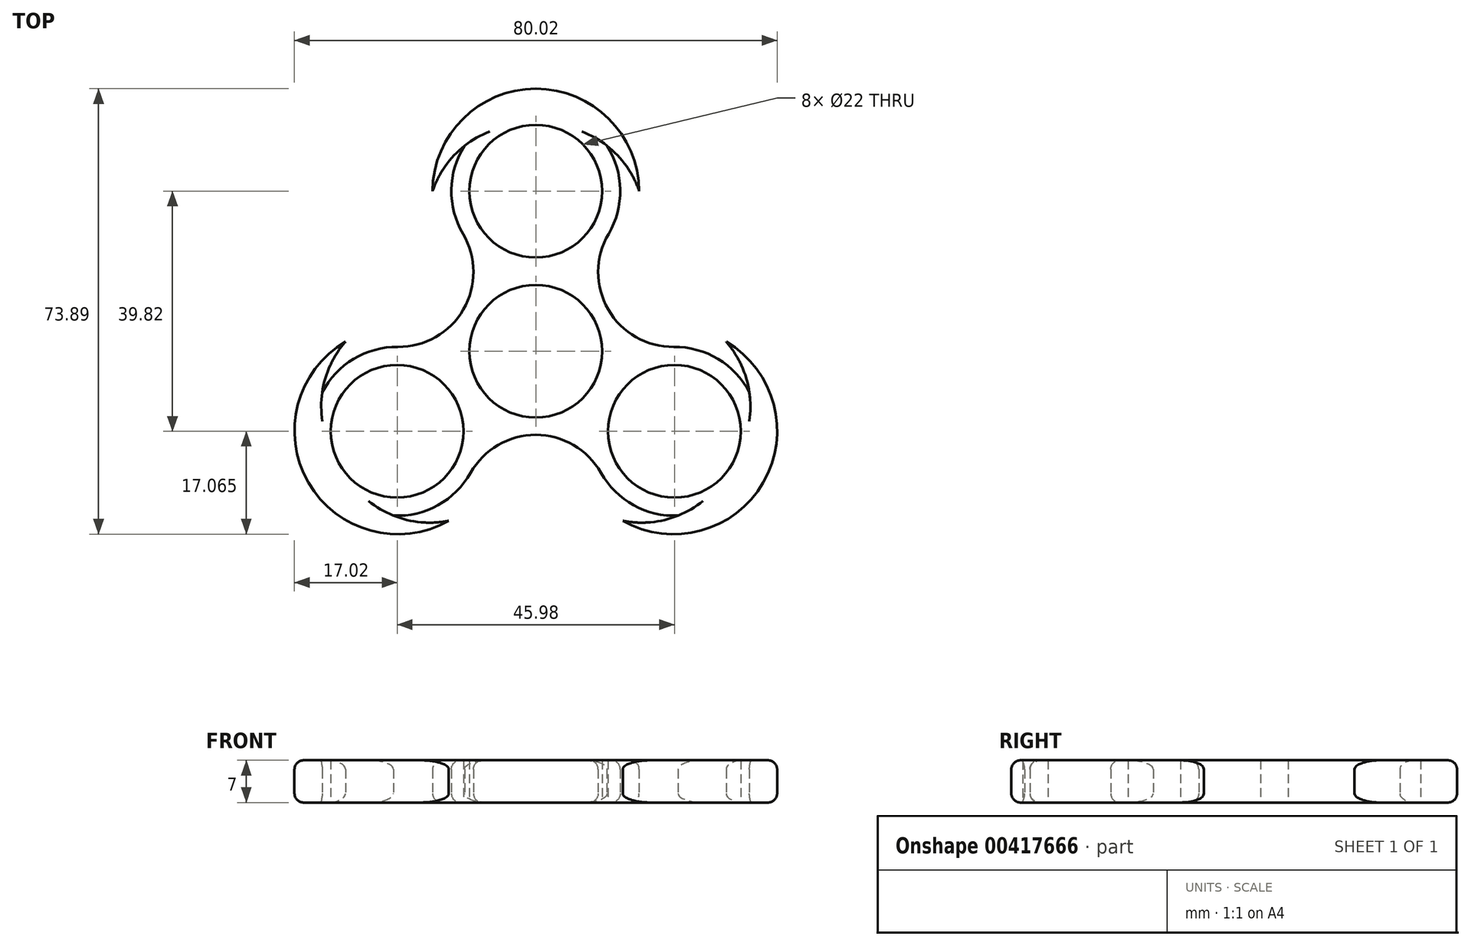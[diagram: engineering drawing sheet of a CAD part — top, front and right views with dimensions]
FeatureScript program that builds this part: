
annotation { "Feature Type Name" : "Feature", "Feature Type Description" : "" }
export const myFeature = defineFeature(function(context is Context, id is Id, definition is map)
    precondition{}
    {
        {
            var Q0;
            Q0=qCreatedBy(makeId("Top.planeOp"),FACE);
            var sketch = newSketch(context, id + "F0", { "sketchPlane" : qUnion([Q0])});
            skPoint(sketch, "E0", {"position": v(-7.78, 43.65) * mm});
            skPoint(sketch, "E1", {"position": v(7.78, 43.65) * mm});
            skLineSegment(sketch, "E2", {"start": v(-11.8, 43.4) * mm, "end": v(-11.8, 43.4) * mm});
            skArc(sketch, "E3", {"start": v(-11.8, 43.4) * mm, "mid": v(-14, 36.12) * mm, "end": v(-12.06, 28.77) * mm});
            skArc(sketch, "E4", {"start": v(7.78, 43.65) * mm, "mid": v(0, 46.88) * mm, "end": v(-7.78, 43.65) * mm});
            skArc(sketch, "E5", {"start": v(-7.78, 43.65) * mm, "mid": v(0, 24.88) * mm, "end": v(7.78, 43.65) * mm});
            skPoint(sketch, "E6.center", {"position": v(0, 0) * mm});
            skPoint(sketch, "E7", {"position": v(0, 56.88) * mm});
            skCircle(sketch, "E8", {"center": v(0, 9.33) * mm, "radius": 11 * mm});
            skArc(sketch, "E9.1.0", {"start": v(-23.6, -17.93) * mm, "mid": v(-16.2, -16.2) * mm, "end": v(-10.8, -10.84) * mm});
            skArc(sketch, "E9.1.1", {"start": v(-25.84, -14.57) * mm, "mid": v(-13.46, 1.55) * mm, "end": v(-33.62, -1.1) * mm});
            skArc(sketch, "E9.1.2", {"start": v(-33.62, -1.1) * mm, "mid": v(-32.52, -9.45) * mm, "end": v(-25.84, -14.57) * mm});
            skArc(sketch, "E9.2.0", {"start": v(35.41, 2.51) * mm, "mid": v(30.2, 8.05) * mm, "end": v(22.87, 10.05) * mm});
            skArc(sketch, "E9.2.1", {"start": v(33.62, -1.1) * mm, "mid": v(13.46, 1.55) * mm, "end": v(25.84, -14.57) * mm});
            skArc(sketch, "E9.2.2", {"start": v(25.84, -14.57) * mm, "mid": v(32.52, -9.45) * mm, "end": v(33.62, -1.1) * mm});
            skArc(sketch, "E10", {"start": v(8.99, 30.58) * mm, "mid": v(8.87, 29.9) * mm, "end": v(8.77, 29.24) * mm});
            skArc(sketch, "E11.1.0", {"start": v(13.91, -9.08) * mm, "mid": v(13.4, -8.64) * mm, "end": v(12.86, -8.22) * mm});
            skLineSegment(sketch, "E11.anchor1", {"start": v(0, 9.33) * mm, "end": v(22.9, 6.48) * mm, "construction": true});
            skLineSegment(sketch, "E11.anchor2", {"start": v(0, 9.33) * mm, "end": v(-8.99, 30.58) * mm, "construction": true});
            skLineSegment(sketch, "E12", {"start": v(0, 35.87) * mm, "end": v(8.99, 30.58) * mm});
            skLineSegment(sketch, "E13", {"start": v(8.99, 30.58) * mm, "end": v(9.48, 30.3) * mm});
            skLineSegment(sketch, "E14.MirrorCS", {"start": v(0, 35.87) * mm, "end": v(-8.99, 30.58) * mm});
            skLineSegment(sketch, "E15.1.0", {"start": v(-23, -3.95) * mm, "end": v(-22.9, 6.48) * mm});
            skLineSegment(sketch, "E15.1.1", {"start": v(-23, -3.95) * mm, "end": v(-13.91, -9.08) * mm});
            skLineSegment(sketch, "E15.1.2", {"start": v(-13.91, -9.08) * mm, "end": v(-13.42, -9.36) * mm});
            skLineSegment(sketch, "E15.1.3", {"start": v(-22.9, 6.48) * mm, "end": v(-22.87, 10.05) * mm});
            skLineSegment(sketch, "E15.2.0", {"start": v(23, -3.95) * mm, "end": v(13.91, -9.08) * mm});
            skLineSegment(sketch, "E15.2.1", {"start": v(23, -3.95) * mm, "end": v(22.9, 6.48) * mm});
            skLineSegment(sketch, "E15.2.2", {"start": v(22.9, 6.48) * mm, "end": v(22.87, 10.05) * mm});
            skLineSegment(sketch, "E15.2.3", {"start": v(13.91, -9.08) * mm, "end": v(10.8, -10.84) * mm});
            skArc(sketch, "E16.trimOffspring", {"start": v(-8.66, 24.88) * mm, "mid": v(-7.3, 23.93) * mm, "end": v(-5.85, 23.15) * mm});
            skArc(sketch, "E17.trimOffspring", {"start": v(-22.87, 10.05) * mm, "mid": v(-30.2, 8.05) * mm, "end": v(-35.41, 2.51) * mm});
            skArc(sketch, "E18", {"start": v(-12.06, 28.77) * mm, "mid": v(-12, 16.26) * mm, "end": v(-22.87, 10.05) * mm});
            skArc(sketch, "E19.trimOffspring", {"start": v(12.06, 28.77) * mm, "mid": v(14, 36.12) * mm, "end": v(11.8, 43.4) * mm});
            skArc(sketch, "E20.trimOffspring", {"start": v(21.63, 6.97) * mm, "mid": v(22.26, 6.72) * mm, "end": v(22.9, 6.48) * mm});
            skArc(sketch, "E21.trimOffspring", {"start": v(-12.86, -8.22) * mm, "mid": v(-13.4, -8.64) * mm, "end": v(-13.91, -9.08) * mm});
            skArc(sketch, "E22.trimOffspring", {"start": v(10.8, -10.84) * mm, "mid": v(16.2, -16.2) * mm, "end": v(23.6, -17.93) * mm});
            skArc(sketch, "E23", {"start": v(12.06, 28.77) * mm, "mid": v(12, 16.26) * mm, "end": v(22.87, 10.05) * mm});
            skArc(sketch, "E24", {"start": v(-10.8, -10.84) * mm, "mid": v(0, -4.54) * mm, "end": v(10.8, -10.84) * mm});
            skArc(sketch, "E25", {"start": v(-11.8, 43.4) * mm, "mid": v(-15.02, 40.03) * mm, "end": v(-17.14, 35.88) * mm});
            skArc(sketch, "E26.MirrorCS", {"start": v(11.8, 43.4) * mm, "mid": v(15.02, 40.03) * mm, "end": v(17.14, 35.88) * mm});
            skLineSegment(sketch, "E27", {"start": v(0, 35.88) * mm, "end": v(0, 46.88) * mm});
            skLineSegment(sketch, "E28", {"start": v(0, 46.88) * mm, "end": v(0, 52.88) * mm});
            skArc(sketch, "E29", {"start": v(17.14, 35.88) * mm, "mid": v(0, 52.88) * mm, "end": v(-17.14, 35.88) * mm});
            skArc(sketch, "E30.1.0", {"start": v(-31.56, 10.9) * mm, "mid": v(-37.71, -12.45) * mm, "end": v(-14.42, -18.79) * mm});
            skArc(sketch, "E30.1.1", {"start": v(-35.41, 2.51) * mm, "mid": v(-34.1, 6.98) * mm, "end": v(-31.56, 10.9) * mm});
            skArc(sketch, "E30.1.2", {"start": v(-23.6, -17.93) * mm, "mid": v(-19.08, -19.03) * mm, "end": v(-14.42, -18.79) * mm});
            skArc(sketch, "E30.2.0", {"start": v(14.42, -18.79) * mm, "mid": v(37.71, -12.45) * mm, "end": v(31.56, 10.9) * mm});
            skArc(sketch, "E30.2.1", {"start": v(23.6, -17.93) * mm, "mid": v(19.08, -19.03) * mm, "end": v(14.42, -18.79) * mm});
            skArc(sketch, "E30.2.2", {"start": v(35.41, 2.51) * mm, "mid": v(34.1, 6.98) * mm, "end": v(31.56, 10.9) * mm});
            skSolve(sketch);
        }
        {
            var Q0;
            Q0=makeQuery(id+"F0.imprint","IMPRINT",FACE,{"disambiguationData":[TD([[makeQuery(id+"F0.imprint","IMPRINT",EDGE,{"derivedFrom":sQuery(id+"F0.wireOp",EDGE,"E8")}),-1.0]])]});
            var Q1;
            {var subQ0=sQuery(id+"F0.wireOp",EDGE,"E11.2.0");var subQ1=sQuery(id+"F0.wireOp",EDGE,"E3");var subQ2=makeQuery(id+"F0.imprint","INTERSECT",VERTEX,{"derivedFrom":[subQ1,subQ0]});Q1=makeQuery(id+"F0.imprint","IMPRINT",FACE,{"disambiguationData":[TD([[makeQuery(id+"F0.imprint","IMPRINT",EDGE,{"disambiguationData":[TD([[subQ2,-1.0]])],"derivedFrom":subQ1}),1.0]])]});}
            var Q2;
            {var subQ5=sQuery(id+"F0.wireOp",EDGE,"rF4rL3q0-zzDa-D3dE-KOLq-3nMpvaDNyaDo");Q2=makeQuery(id+"F0.imprint","IMPRINT",FACE,{"disambiguationData":[TD([[makeQuery(id+"F0.imprint","IMPRINT",EDGE,{"derivedFrom":subQ5}),1.0]])]});}
            var Q3;
            {var subQ1=sQuery(id+"F0.wireOp",EDGE,"bc3d388e-9ec0-4d8b-95e0-a7e616ce30ed0.MirrorCS");var subQ3=sQuery(id+"F0.wireOp",EDGE,"E3");var subQ4=makeQuery(id+"F0.imprint","INTERSECT",VERTEX,{"derivedFrom":[subQ1,subQ3]});Q3=makeQuery(id+"F0.imprint","IMPRINT",FACE,{"disambiguationData":[TD([[makeQuery(id+"F0.imprint","IMPRINT",EDGE,{"disambiguationData":[TD([[subQ4,1.0]])],"derivedFrom":subQ3}),1.0]])]});}
            var Q4;
            {var subQ1=sQuery(id+"F0.wireOp",EDGE,"E9.2.2");Q4=makeQuery(id+"F0.imprint","IMPRINT",FACE,{"disambiguationData":[TD([[makeQuery(id+"F0.imprint","IMPRINT",EDGE,{"derivedFrom":subQ1}),-1.0]])]});}
            var Q5;
            {var subQ0=sQuery(id+"F0.wireOp",EDGE,"E9.2.5");var subQ1=sQuery(id+"F0.wireOp",EDGE,"E9.2.0");var subQ2=makeQuery(id+"F0.imprint","INTERSECT",VERTEX,{"derivedFrom":[subQ1,subQ0]});Q5=makeQuery(id+"F0.imprint","IMPRINT",FACE,{"disambiguationData":[TD([[makeQuery(id+"F0.imprint","IMPRINT",EDGE,{"disambiguationData":[TD([[subQ2,1.0]])],"derivedFrom":subQ1}),1.0]])]});}
            var Q6;
            {var subQ0=sQuery(id+"F0.wireOp",EDGE,"E10");var subQ1=sQuery(id+"F0.wireOp",EDGE,"E9.2.0");var subQ2=makeQuery(id+"F0.imprint","INTERSECT",VERTEX,{"derivedFrom":[subQ1,subQ0]});Q6=makeQuery(id+"F0.imprint","IMPRINT",FACE,{"disambiguationData":[TD([[makeQuery(id+"F0.imprint","IMPRINT",EDGE,{"disambiguationData":[TD([[subQ2,-1.0]])],"derivedFrom":subQ1}),1.0]])]});}
            var Q7;
            {var subQ1=sQuery(id+"F0.wireOp",EDGE,"E9.1.2");Q7=makeQuery(id+"F0.imprint","IMPRINT",FACE,{"disambiguationData":[TD([[makeQuery(id+"F0.imprint","IMPRINT",EDGE,{"derivedFrom":subQ1}),-1.0]])]});}
            var Q8;
            {var subQ0=sQuery(id+"F0.wireOp",EDGE,"E9.1.5");var subQ1=sQuery(id+"F0.wireOp",EDGE,"E9.1.0");var subQ2=makeQuery(id+"F0.imprint","INTERSECT",VERTEX,{"derivedFrom":[subQ1,subQ0]});Q8=makeQuery(id+"F0.imprint","IMPRINT",FACE,{"disambiguationData":[TD([[makeQuery(id+"F0.imprint","IMPRINT",EDGE,{"disambiguationData":[TD([[subQ2,1.0]])],"derivedFrom":subQ1}),1.0]])]});}
            var Q9;
            {var subQ0=sQuery(id+"F0.wireOp",EDGE,"E11.1.0");var subQ1=sQuery(id+"F0.wireOp",EDGE,"E9.1.0");var subQ2=makeQuery(id+"F0.imprint","INTERSECT",VERTEX,{"derivedFrom":[subQ1,subQ0]});Q9=makeQuery(id+"F0.imprint","IMPRINT",FACE,{"disambiguationData":[TD([[makeQuery(id+"F0.imprint","IMPRINT",EDGE,{"disambiguationData":[TD([[subQ2,-1.0]])],"derivedFrom":subQ1}),1.0]])]});}
            extrude(context, id + "F1", {"entities" : qUnion([Q0, Q1, Q2, Q3, Q4, Q5, Q6, Q7, Q8, Q9]), "endBound" : BoundingType.SYMMETRIC, "depth" : 7 * mm});
        }
        {
            var Q0;
            Q0=makeQuery(id+"F1.opExtrude","CAP_EDGE",EDGE,{"disambiguationData":[OSD([sQuery(id+"F0.wireOp",EDGE,"E30.2.0")])],"isStart":false});
            var Q1;
            Q1=makeQuery(id+"F1.opExtrude","CAP_EDGE",EDGE,{"disambiguationData":[OSD([sQuery(id+"F0.wireOp",EDGE,"E22.trimOffspring")])],"isStart":false});
            var Q2;
            Q2=makeQuery(id+"F1.opExtrude","CAP_EDGE",EDGE,{"disambiguationData":[OSD([sQuery(id+"F0.wireOp",EDGE,"E30.1.0")])],"isStart":false});
            var Q3;
            Q3=makeQuery(id+"F1.opExtrude","CAP_EDGE",EDGE,{"disambiguationData":[OSD([sQuery(id+"F0.wireOp",EDGE,"E17.trimOffspring")])],"isStart":false});
            var Q4;
            Q4=makeQuery(id+"F1.opExtrude","CAP_EDGE",EDGE,{"disambiguationData":[OSD([sQuery(id+"F0.wireOp",EDGE,"E29")])],"isStart":false});
            var Q5;
            Q5=makeQuery(id+"F1.opExtrude","CAP_EDGE",EDGE,{"disambiguationData":[OSD([sQuery(id+"F0.wireOp",EDGE,"E19.trimOffspring")])],"isStart":false});
            fillet(context, id + "F2", {"entities" : qUnion([Q0, Q1, Q2, Q3, Q4, Q5]), "radius" : 1.5 * mm, "tangentPropagation" : true, "allowEdgeOverflow" : false});
        }
        {
            var Q0;
            Q0=makeQuery(id+"F1.opExtrude","CAP_EDGE",EDGE,{"disambiguationData":[OSD([sQuery(id+"F0.wireOp",EDGE,"E30.2.0")])],"isStart":true});
            var Q1;
            Q1=makeQuery(id+"F1.opExtrude","CAP_EDGE",EDGE,{"disambiguationData":[OSD([sQuery(id+"F0.wireOp",EDGE,"E22.trimOffspring")])],"isStart":true});
            var Q2;
            Q2=makeQuery(id+"F1.opExtrude","CAP_EDGE",EDGE,{"disambiguationData":[OSD([sQuery(id+"F0.wireOp",EDGE,"E30.1.0")])],"isStart":true});
            var Q3;
            Q3=makeQuery(id+"F1.opExtrude","CAP_EDGE",EDGE,{"disambiguationData":[OSD([sQuery(id+"F0.wireOp",EDGE,"E17.trimOffspring")])],"isStart":true});
            var Q4;
            Q4=makeQuery(id+"F1.opExtrude","CAP_EDGE",EDGE,{"disambiguationData":[OSD([sQuery(id+"F0.wireOp",EDGE,"E29")])],"isStart":true});
            var Q5;
            Q5=makeQuery(id+"F1.opExtrude","CAP_EDGE",EDGE,{"disambiguationData":[OSD([sQuery(id+"F0.wireOp",EDGE,"E19.trimOffspring")])],"isStart":true});
            fillet(context, id + "F3", {"entities" : qUnion([Q0, Q1, Q2, Q3, Q4, Q5]), "radius" : 1.5 * mm, "tangentPropagation" : true, "allowEdgeOverflow" : false});
        }
    });
